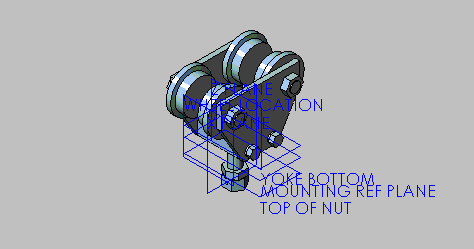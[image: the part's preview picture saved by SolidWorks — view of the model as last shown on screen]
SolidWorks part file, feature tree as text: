
SOLIDWORKS PART (.sldprt)
format: sldprt  version: not decoded by parser v0  size: 1,606,144 bytes
history: native  units: mm
features: sketch x13, extrude x11, plane x10, mirror x5, material x1, chamfer x1, cut_extrude x1, revolve x1 (+10 scaffold rows collapsed)
feature tree (53):
  scaffold x10  (default folders/planes/origin — collapsed)
  material  "Material <not specified>"
  plane  "Z PLANE"  Offset=0mm
  plane  "YOKE BOTTOM"  Offset=0mm
  plane  "X PLANE"  Offset=0mm
  sketch  "YOKE CROSS SECTION"  dims[D1=44.45mm D2=114.3mm]
  plane  "1/2 YOKE LENGTH (A)"  Offset=71.4375mm
  plane  "WHEEL LOCATION"  Offset=95.25mm
  extrude  "YOKE"  [1 undecoded]
  sketch  "SIDEPLATE PROFILE"  dims[D1=57.15mm D2=76.2mm D3=76.2mm D4=57.15mm D5=76.2mm D6=76.2mm D7=266.7mm D8=~128.517772mm D9=~128.517772mm D10=203.2mm D11=203.2mm]
  plane  "WHEEL HEIGHT"  Offset=155.575mm
  plane  "YOKE SCREW LOCATION Z"  Offset=38.1mm
  plane  "YOKE SCREW LOCATION Y"  Offset=25.4mm
  extrude  "SIDEPLATE"  Depth=15.875mm
  sketch  "WHEEL PIN NUT PROFILE"  dims[D1=50.8mm D2=47.625mm]
  extrude  "WHEEL PIN NUT"  Depth=20.701mm
  sketch  "WHEEL PIN PROJECTION PROFILE"  dims[D1=34.925mm D2=47.625mm]
  extrude  "WHEEL PIN PROJECTION"  Depth=3.175mm
  sketch  "LOCKNUTS PROFILE"  dims[D1=31.75mm]
  extrude  "LOCKNUTS"  Depth=5.5626mm
  sketch  "SCREWS PROFILE"  dims[D1=31.75mm]
  extrude  "SCREWS"  Depth=15.3416mm
  sketch  "PROFILE"  dims[D1=57.15mm]
  extrude  "KING BOLT HEAD"  Depth=31.75mm
  mirror  "Mirror1"
  mirror  "Mirror YOKE SCREWS"
  mirror  "Mirror SIDE 1"
  plane  "TOP OF NUT"  Offset=83.052101mm
  sketch  "DIA."  dims[D1=38.1mm]
  extrude  "KING BOLT"  [1 undecoded]
  sketch  "KING BOLT JAN NUT PROFILE"  dims[D1=57.15mm]
  extrude  "KING BOLT JAM NUT"  Depth=21.43125mm
  sketch  "KING BOLT NUT PROFILE"  dims[c1.D1=57.15mm c1.D2=44.45mm c2.D1=0.0mm]
  extrude  "KING BOLT NUT"  Depth=33.3375mm
  sketch  "Sketch5"
  extrude  "EXTENDED KING BOLT"  Depth=6.35mm
  chamfer  "Chamfer1"  Distance=2.38125mm Angle=45deg
  plane  "MOUNTING REF PLANE"  Offset=34.925mm
  sketch  "Sketch11"  dims[D1=6.6802mm D2=~16.66875mm]
  cut_extrude  "COTTER PIN HOLE"  [1 undecoded]
  sketch  "Sketch12"  dims[c1.D12=88.9mm c1.D1=1.5875mm c1.D2=46.0375mm c1.D3=46.0375mm c1.D4=~17.038518mm c1.D5=19.05mm c1.D6=46.0375mm c1.D7=23.8125mm c1.D8=69.85mm c1.D9=69.85mm c1.D10=57.15mm c1.D11=~52.954692mm c2.D3=1.5875mm c2.D10=~57.076867mm]
  revolve  "WHEEL"  Angle=360deg
  mirror  "Mirror2"
  mirror  "Mirror3"  TREADED ROD NUT=9.525mm
decode coverage: 24 of 32 modeling features carry decoded parameters
note: ~ marks probable driven/reference dimensions
note: 3 parameter values undecoded
summary: no parameter record found for 3 features
note: suppression state not decoded; provenance and decode notes live in map.json
